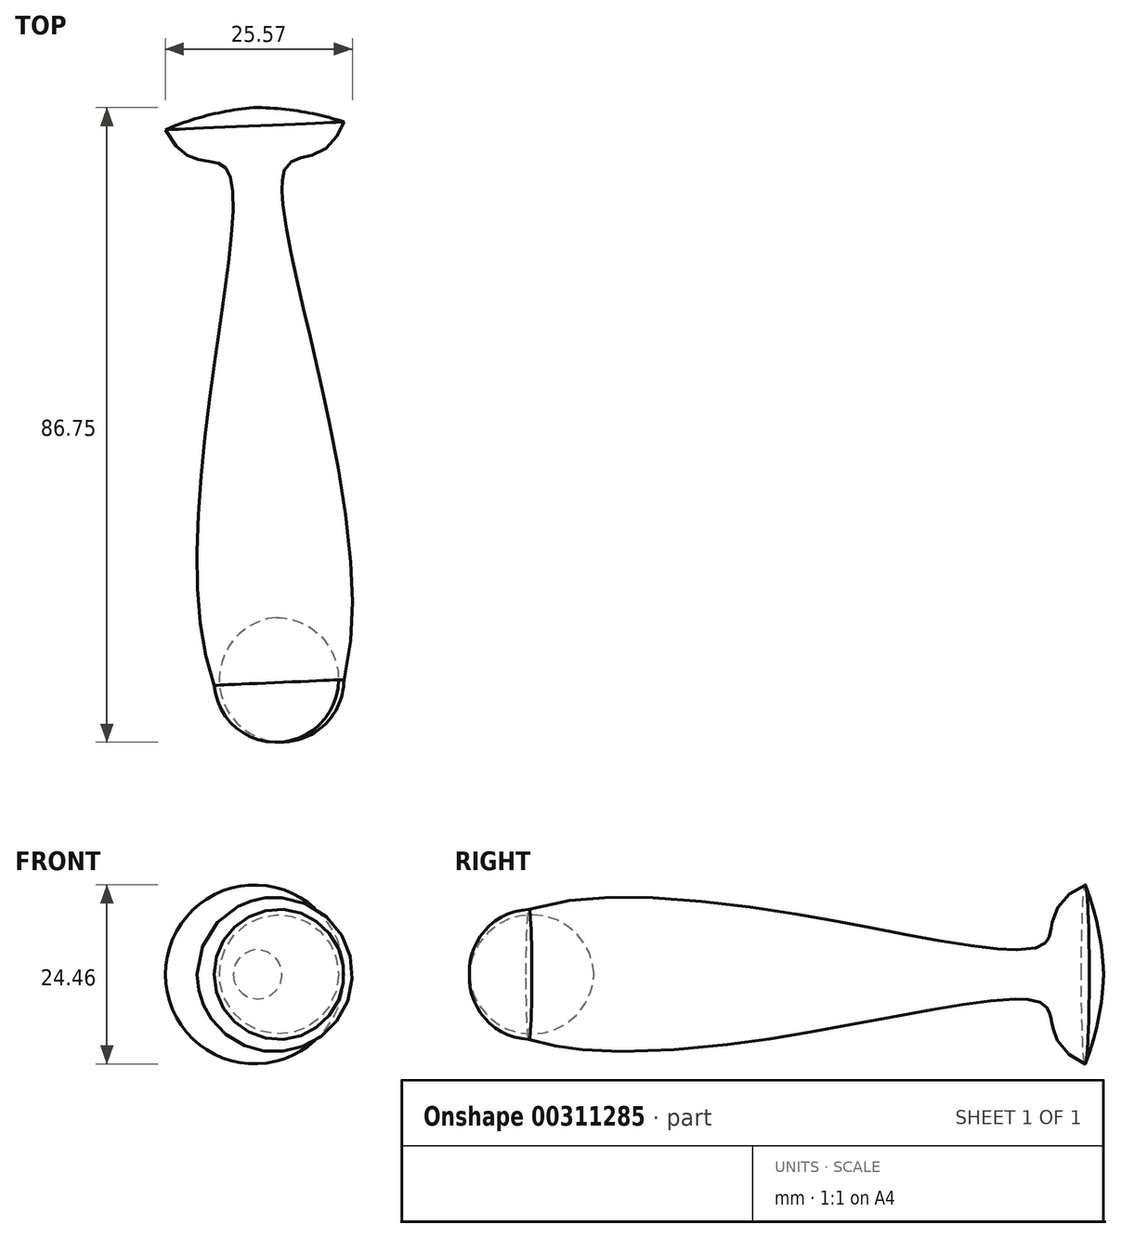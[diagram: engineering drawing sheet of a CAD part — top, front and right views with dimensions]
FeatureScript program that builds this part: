
annotation { "Feature Type Name" : "Feature", "Feature Type Description" : "" }
export const myFeature = defineFeature(function(context is Context, id is Id, definition is map)
    precondition{}
    {
        {
            var Q0;
            Q0=qCreatedBy(makeId("Top.planeOp"),FACE);
            var sketch = newSketch(context, id + "F0", { "sketchPlane" : qUnion([Q0])});
            skArc(sketch, "E0", {"start": v(-17.05, 0) * mm, "mid": v(-8.53, -8.53) * mm, "end": v(0, 0) * mm});
            skArc(sketch, "E1", {"start": v(0, 76.23) * mm, "mid": v(-12.32, 78.2) * mm, "end": v(-24.65, 76.23) * mm});
            skLineSegment(sketch, "E2", {"start": v(-12.32, 78.2) * mm, "end": v(-8.53, -8.53) * mm});
            skFitSpline(sketch, "E3", {"points": [v(-17.05, 0) * mm, v(-17.05, 71.04) * mm, v(-24.65, 76.23) * mm], "startDerivative": vector(-17.61, 84.64) * mm, "endDerivative": vector(-2.1, 41.17) * mm});
            skFitSpline(sketch, "E4", {"points": [v(0, 0) * mm, v(-7.99, 69.97) * mm, v(0, 76.23) * mm], "startDerivative": vector(23.23, 90.35) * mm, "endDerivative": vector(25.88, 68.34) * mm});
            skSolve(sketch);
        }
        {
            var Q0;
            {var subQ2=sQuery(id+"F0.wireOp",EDGE,"E2");Q0=makeQuery(id+"F0.imprint","IMPRINT",FACE,{"disambiguationData":[TD([[makeQuery(id+"F0.imprint","IMPRINT",EDGE,{"derivedFrom":subQ2}),1.0]])]});}
            var Q1;
            Q1=sQuery(id+"F0.wireOp",EDGE,"E2");
            revolve(context, id + "F1", {"entities" : qUnion([Q0]), "axis" : qUnion([Q1]), "revolveType" : RevolveType.FULL});
        }
    });
